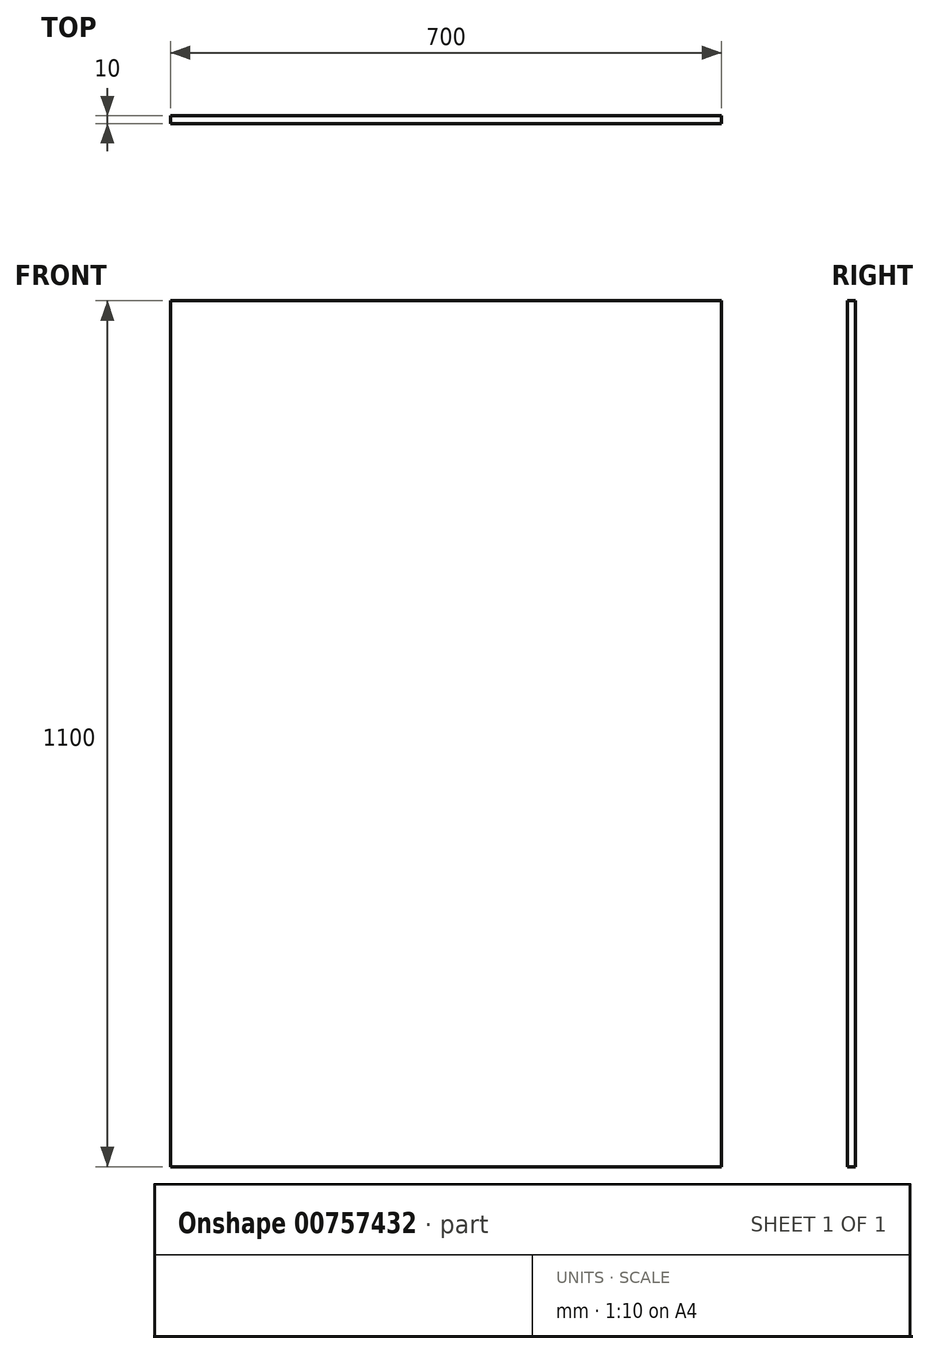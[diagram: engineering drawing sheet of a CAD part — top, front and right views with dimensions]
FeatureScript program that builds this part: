
annotation { "Feature Type Name" : "Feature", "Feature Type Description" : "" }
export const myFeature = defineFeature(function(context is Context, id is Id, definition is map)
    precondition{}
    {
        {
            var Q0;
            Q0=qCreatedBy(makeId("Front.planeOp"),FACE);
            var sketch = newSketch(context, id + "F0", { "sketchPlane" : qUnion([Q0])});
            skLineSegment(sketch, "E0.bottom", {"start": v(-350, 550) * mm, "end": v(350, 550) * mm});
            skLineSegment(sketch, "E0.top", {"start": v(-350, -550) * mm, "end": v(350, -550) * mm});
            skLineSegment(sketch, "E0.left", {"start": v(-350, 550) * mm, "end": v(-350, -550) * mm});
            skLineSegment(sketch, "E0.right", {"start": v(350, 550) * mm, "end": v(350, -550) * mm});
            skSolve(sketch);
        }
        {
            var Q0;
            Q0=makeQuery(id+"F0.imprint","IMPRINT",FACE,{"disambiguationData":[TD([[makeQuery(id+"F0.imprint","IMPRINT",EDGE,{"derivedFrom":sQuery(id+"F0.wireOp",EDGE,"E0.bottom")}),-1.0]])]});
            extrude(context, id + "F1", {"entities" : qUnion([Q0]), "depth" : 10 * mm, "offsetDistance" : 25 * mm});
        }
    });
